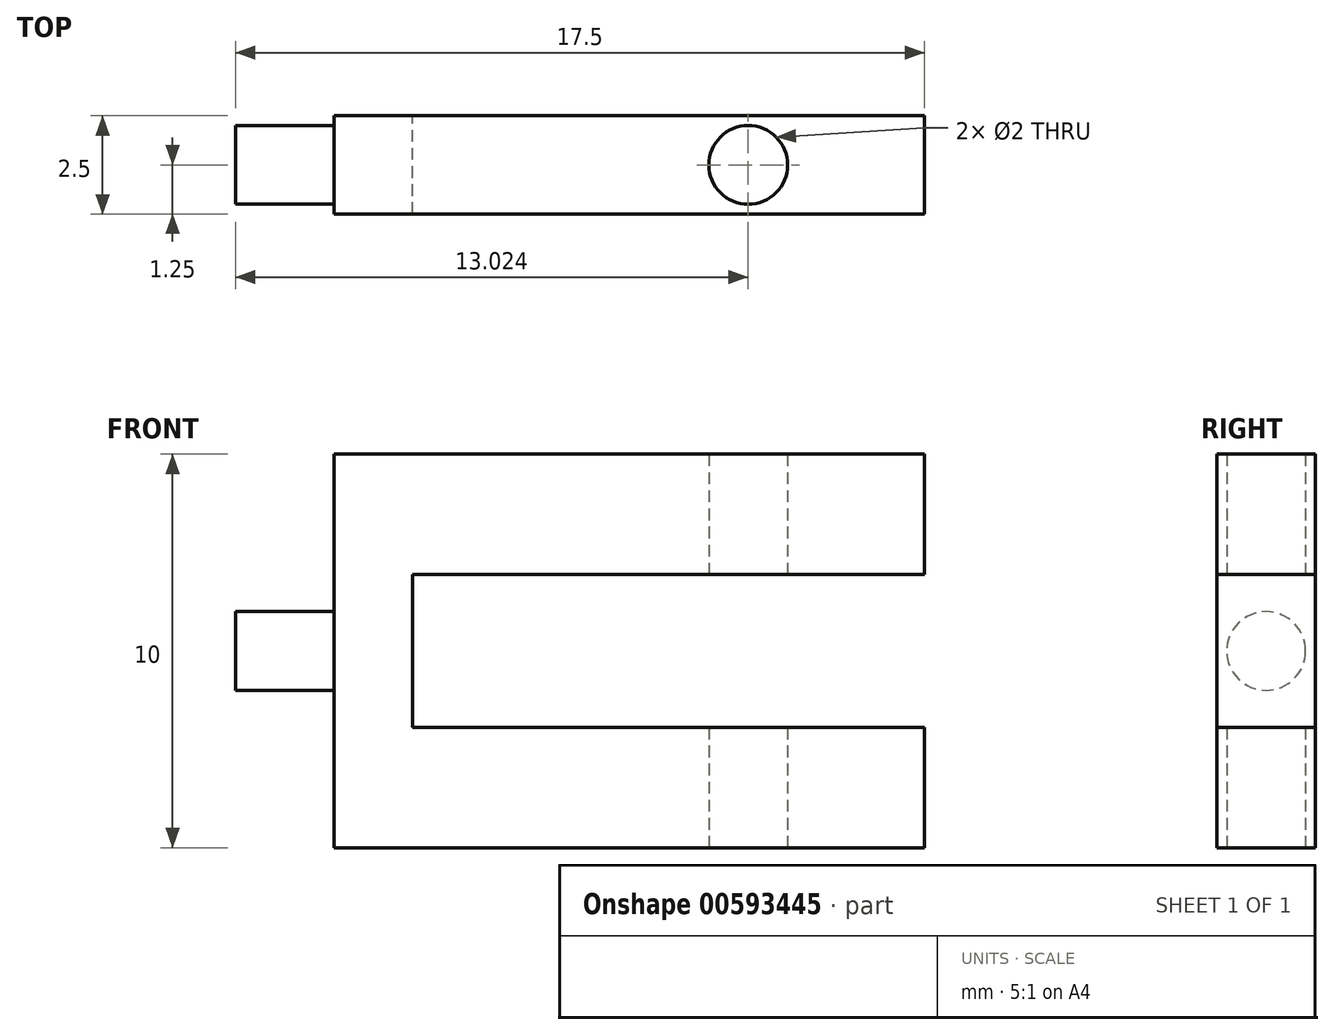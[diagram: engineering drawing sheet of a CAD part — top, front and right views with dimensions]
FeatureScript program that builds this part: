
annotation { "Feature Type Name" : "Feature", "Feature Type Description" : "" }
export const myFeature = defineFeature(function(context is Context, id is Id, definition is map)
    precondition{}
    {
        {
            assignVariable(context, id + "F0", {"name" : "Size_hole", "anyValue" : 2});
        }
        {
            assignVariable(context, id + "F1", {"name" : "depth", "anyValue" : 2.5});
        }
        {
            var Q0;
            Q0=qCreatedBy(makeId("Front.planeOp"),FACE);
            var sketch = newSketch(context, id + "F2", { "sketchPlane" : qUnion([Q0])});
            skLineSegment(sketch, "E0.bottom", {"start": v(-4.06, 5) * mm, "end": v(10.94, 5) * mm});
            skLineSegment(sketch, "E0.top", {"start": v(-4.06, 1.94) * mm, "end": v(10.94, 1.94) * mm});
            skLineSegment(sketch, "E0.left", {"start": v(-4.06, 5) * mm, "end": v(-4.06, 1.94) * mm});
            skLineSegment(sketch, "E0.right", {"start": v(10.94, 5) * mm, "end": v(10.94, 1.94) * mm});
            skLineSegment(sketch, "E1.bottom", {"start": v(-4.06, 5) * mm, "end": v(-0.06, 5) * mm});
            skLineSegment(sketch, "E2.MirrorCS", {"start": v(-4.06, -5) * mm, "end": v(10.94, -5) * mm});
            skLineSegment(sketch, "E3.MirrorCS", {"start": v(10.94, -5) * mm, "end": v(10.94, -1.94) * mm});
            skLineSegment(sketch, "E4.MirrorCS", {"start": v(-4.06, -5) * mm, "end": v(-0.06, -5) * mm});
            skLineSegment(sketch, "E5.MirrorCS", {"start": v(-4.06, -5) * mm, "end": v(-4.06, -1.94) * mm});
            skLineSegment(sketch, "E6.MirrorCS", {"start": v(-4.06, -1.94) * mm, "end": v(10.94, -1.94) * mm});
            skLineSegment(sketch, "E7", {"start": v(-4.06, 5) * mm, "end": v(-4.06, -5) * mm});
            skLineSegment(sketch, "E8", {"start": v(-2.06, 5) * mm, "end": v(-2.06, -5) * mm});
            skSolve(sketch);
        }
        {
            var Q0;
            Q0 = qSketchRegion(id + "F2", true);
            extrude(context, id + "F3", {"entities" : qUnion([Q0]), "depth" : 2.5 * mm, "offsetDistance" : 25 * mm});
        }
        {
            var Q0;
            Q0=makeQuery(id+"F3.opExtrude","SWEPT_FACE",FACE,{"disambiguationData":[OSD([sQuery(id+"F2.wireOp",EDGE,"E2.MirrorCS"),sQuery(id+"F2.wireOp",EDGE,"E4.MirrorCS")])]});
            var sketch = newSketch(context, id + "F4", { "sketchPlane" : qUnion([Q0])});
            skPoint(sketch, "E9", {"position": v(6.46, 1.25) * mm});
            skPoint(sketch, "E9.positionSnap0", {"position": v(10.94, 1.25) * mm});
            skSolve(sketch);
        }
        {
            var Q0;
            Q0=sQuery(id+"F4.wireOp",VERTEX,"E9");
            var Q1;
            Q1=makeQuery(id+"F3.opExtrude","SWEPT_BODY",BODY,{"disambiguationData":[OSD([sQuery(id+"F2.wireOp",EDGE,"E0.bottom"),sQuery(id+"F2.wireOp",EDGE,"E0.top"),sQuery(id+"F2.wireOp",EDGE,"E0.right"),sQuery(id+"F2.wireOp",EDGE,"E1.bottom"),sQuery(id+"F2.wireOp",EDGE,"E2.MirrorCS"),sQuery(id+"F2.wireOp",EDGE,"E3.MirrorCS"),sQuery(id+"F2.wireOp",EDGE,"E4.MirrorCS"),sQuery(id+"F2.wireOp",EDGE,"E6.MirrorCS"),sQuery(id+"F2.wireOp",EDGE,"E7"),sQuery(id+"F2.wireOp",EDGE,"E8")])]});
            hole(context, id + "F5", {"style" : HoleStyle.SIMPLE, "endStyle" : HoleEndStyle.THROUGH, "holeDiameter" : (getVariable(context, 'Size_hole')) * mm, "majorDiameter" : 5 * mm, "isTappedThrough" : true, "tappedDepth" : 12.7 * mm, "tapClearance" : 3, "locations" : qUnion([Q0]), "scope" : qUnion([Q1])});
        }
        {
            var Q0;
            Q0=makeQuery(id+"F3.opExtrude","SWEPT_FACE",FACE,{"disambiguationData":[OSD([sQuery(id+"F2.wireOp",EDGE,"E7")])]});
            var sketch = newSketch(context, id + "F6", { "sketchPlane" : qUnion([Q0])});
            skCircle(sketch, "E10", {"center": v(1.25, 0) * mm, "radius": 1 * mm});
            skPoint(sketch, "E10.centerSnap0", {"position": v(1.25, 5) * mm});
            skSolve(sketch);
        }
        {
            var Q0;
            Q0 = qSketchRegion(id + "F6", true);
            extrude(context, id + "F7", {"entities" : qUnion([Q0]), "operationType" : NewBodyOperationType.ADD, "depth" : (getVariable(context, 'depth')) * mm, "offsetDistance" : 25 * mm});
        }
    });
